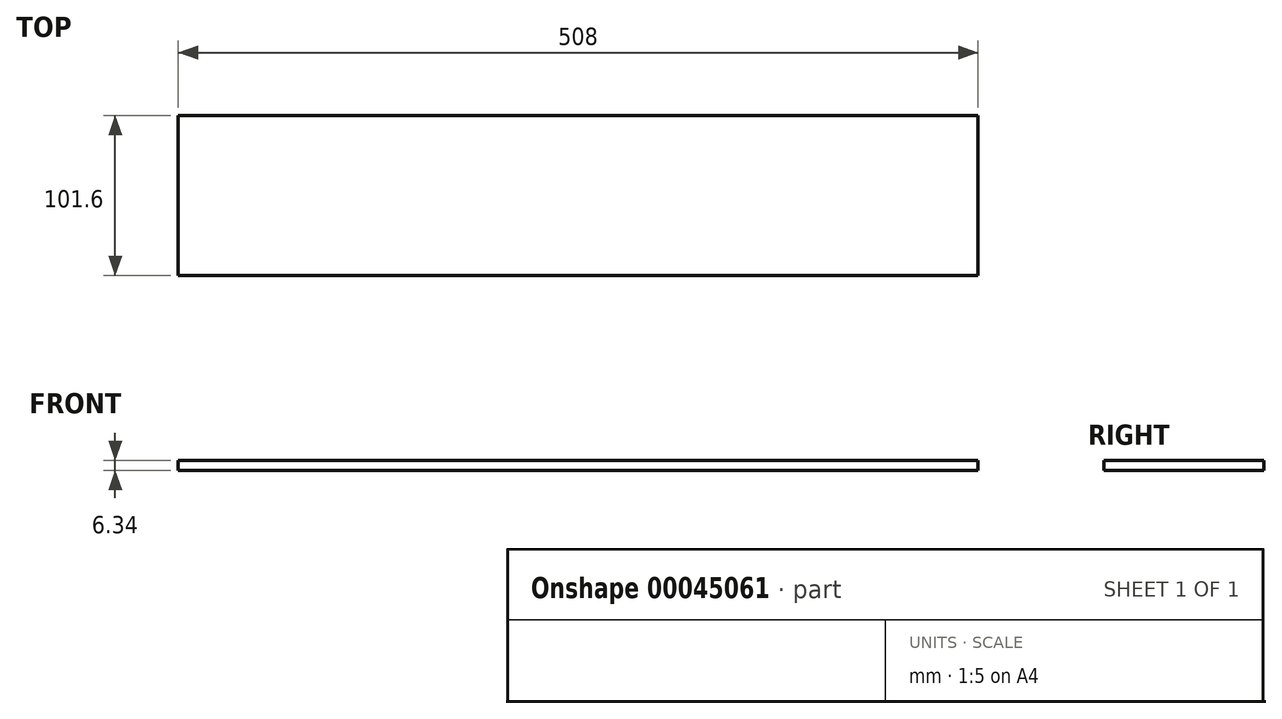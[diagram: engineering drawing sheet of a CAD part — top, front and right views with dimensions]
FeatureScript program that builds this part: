
annotation { "Feature Type Name" : "Feature", "Feature Type Description" : "" }
export const myFeature = defineFeature(function(context is Context, id is Id, definition is map)
    precondition{}
    {
        {
            var Q0;
            Q0=qCreatedBy(makeId("Top.planeOp"),FACE);
            var sketch = newSketch(context, id + "F0", { "sketchPlane" : qUnion([Q0])});
            skLineSegment(sketch, "E0.top", {"start": v(-254, -50.8) * mm, "end": v(254, -50.8) * mm});
            skLineSegment(sketch, "E0.left", {"start": v(-254, 50.8) * mm, "end": v(-254, -50.8) * mm});
            skLineSegment(sketch, "E0.right", {"start": v(254, 50.8) * mm, "end": v(254, -50.8) * mm});
            skLineSegment(sketch, "E1", {"start": v(-254, 50.8) * mm, "end": v(254, 50.8) * mm});
            skSolve(sketch);
        }
        {
            var Q0;
            Q0 = qSketchRegion(id + "F0", true);
            extrude(context, id + "F1", {"entities" : qUnion([Q0]), "endBound" : BoundingType.SYMMETRIC, "depth" : 6.35 * mm});
        }
    });
